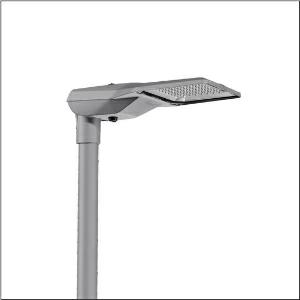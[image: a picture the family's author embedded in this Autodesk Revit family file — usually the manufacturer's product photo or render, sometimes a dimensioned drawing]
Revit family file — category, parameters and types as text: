
# Revit family: streetlight_sl_21_midi___stw1_0a_5xe3e33t08mb_6392
name_source: partatom
category: Lighting Fixtures
units: mm (PartAtom-declared; Revit-internal decimal feet)

## family parameters
Cut with Voids When Loaded = No
Host = Face
Light Source = No
Part Type = Normal
Room Calculation Point = No
Round Connector Dimension = Use Diameter
Shared = No

## types (1)
- --- (1 x LED, 18270 lm, 136 W, 3000K)
    Apparent Load = 136 VA
    CIE Flux Codes = 38 75 98 100 100
    Color Rendering = 70
    Color Temperature = 3000K
    Default Elevation = 1800 mm
    Description = Streetlight SL 21 midi, mast luminaire, primary light control with lens, of PMMA, primary optical cover: cover, of toughened safety glass, transparent, light distribution: STW1.0a, light emission: direct distribution, primary light characteristic: asymmetric, installation type: side-entry, post-top, LED, High Power LED, rated luminous flux: 18.270lm, luminous efficacy: 134lm/W, light colour: 730, colour temperature: 3000K, control: overheat protection, constant luminous flux control, time-dependent luminous flux control, flexible luminous flux parameterisation, presetting dimming logarithmic, mains connection: 230..240V, AC, 50/60Hz, start of lifetime: 136W, end of service life: 142W, reduction: 61W, luminaire housing, of diecast aluminium, powder-coated, Siteco® metallic grey (DB 702S), corrosivity category C5 mid according to DIN EN ISO 12944, please order mast flange separately, inclination adjustable: 0°, 5°, 10°, 15°, sealing non-destructively replaceable, multi-level sealing system, length: 644mm, width: 335mm, height: 110mm, mast flange for spigot size: 42mm (side-entry): 5XC10008XM4, 60/48mm (side-entry/post-top): 5XC10108XM2, 76/60mm (side-entry/post-top): 5XC10108XM1, Smart Interface below and above, protection rating (complete): IP66, insulation class (complete): insulation class II (safety insulation), certification: CE, ENEC, ENEC+, VDE, impact resistance: IK09, permissible operating ambient temperature for outdoor applications: -40..+50°C, standard-compliant lighting for roads and squares, packaging unit: 1 piece

Light Distribution: STW1.0a
    Height = 111 mm
    Lamp = 1 x LED
    Lamp Light Flux = 18270 lm
    Lamp Power = 136 W
    Lamp count = 1
    Length = 644 mm
    Luminous efficacy = 134 lm/W
    Manufacturer = Siteco
    ModVariant = No
    Model = 5XE3E33T08MB
    Number of Poles = 1
    OnlyDefault = Yes
    Power Factor = 1
    Product Name = Streetlight SL 21 midi | STW1.0a
    Product group = mast luminaire | pylon top
    ProductGroupID = 6100
    Protection Class = Protection class II
    Protection Degree = IP 66
    RLX_Detail_Level = 1
    RLX_Emergency_Light_Flux = 0 lm
    RLX_Emergency_Type = 0
    RLX_Emergency_Type_DB = No
    RlxData = <blob elided: 90629 chars, md5=70d30081>
    Socket = socket
    Standby Power = 0 W
    System Light Flux = 18270 lm
    System Power = 136 W
    Type Comments = factory setting: luminous flux: 100 % | dim-lin: 254 | 695 mA
    Type Image = l_1004304.jpg
    URL = http://relux.com
    VarID = @adj_139739
    Voltage = 0 V
    Weight = 0.00 kg
    Width = 336 mm

## geometry (parser evidence)
native form markers: Blend x4, Sweep x10
no freeform markers — native parametric forms only
